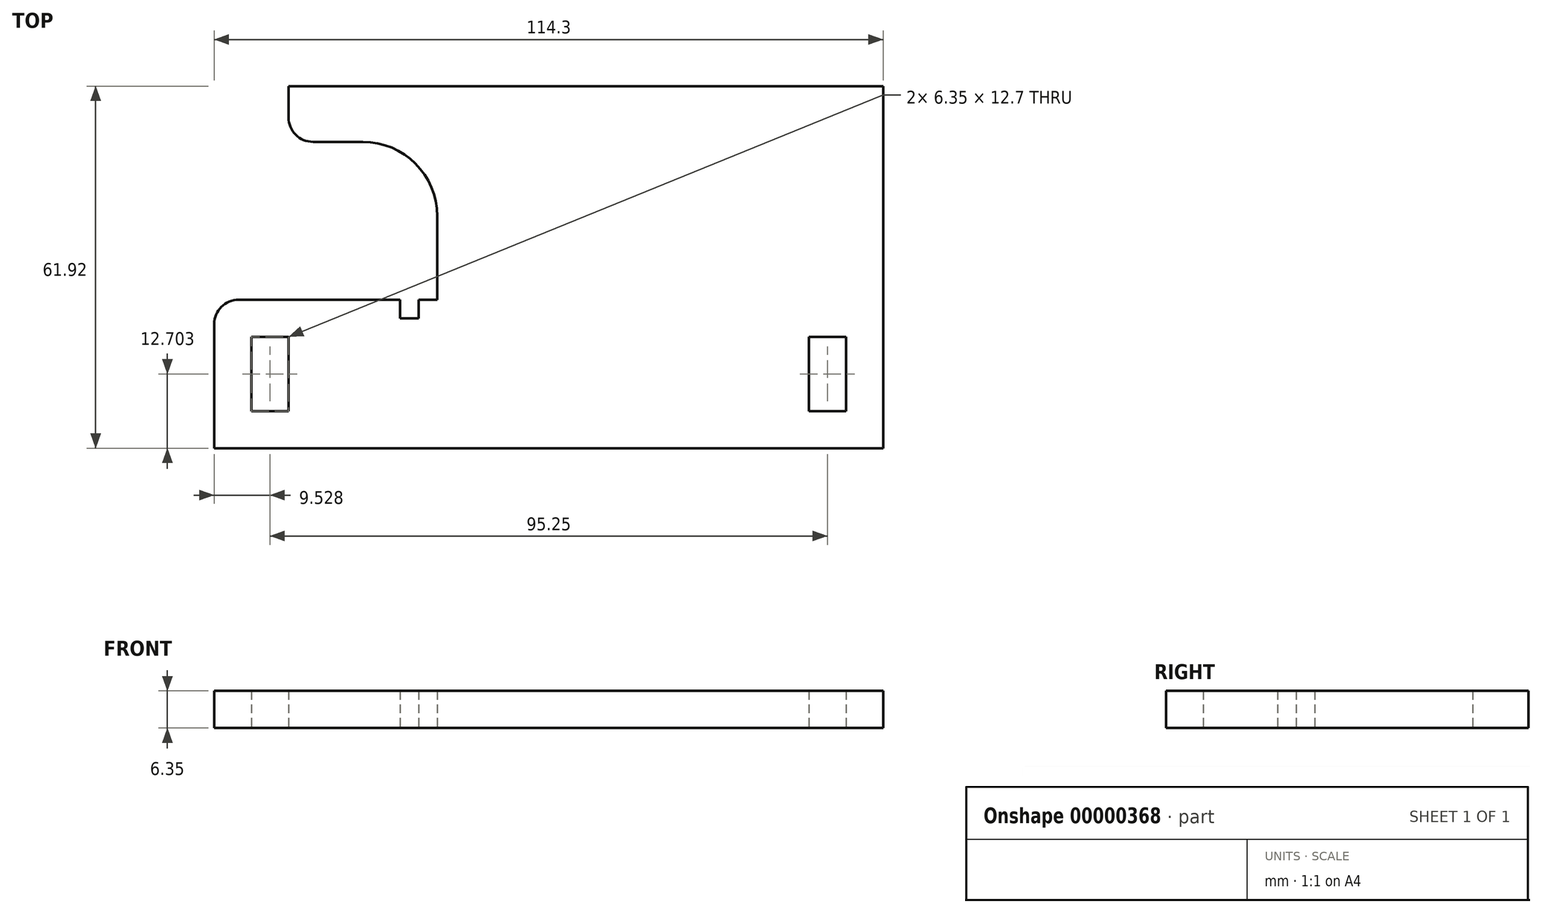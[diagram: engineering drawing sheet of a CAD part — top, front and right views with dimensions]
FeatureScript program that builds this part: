
annotation { "Feature Type Name" : "Feature", "Feature Type Description" : "" }
export const myFeature = defineFeature(function(context is Context, id is Id, definition is map)
    precondition{}
    {
        {
            var Q0;
            Q0=qCreatedBy(makeId("Top.planeOp"),FACE);
            var sketch = newSketch(context, id + "F0", { "sketchPlane" : qUnion([Q0])});
            skLineSegment(sketch, "E0", {"start": v(-52.8, 26.62) * mm, "end": v(48.8, 26.62) * mm});
            skLineSegment(sketch, "E1", {"start": v(48.8, 26.62) * mm, "end": v(48.8, -35.3) * mm});
            skLineSegment(sketch, "E2", {"start": v(48.8, -35.3) * mm, "end": v(-65.5, -35.3) * mm});
            skLineSegment(sketch, "E3", {"start": v(-65.5, -35.3) * mm, "end": v(-65.5, -14.09) * mm});
            skLineSegment(sketch, "E4", {"start": v(-61.3, -9.9) * mm, "end": v(-33.75, -9.9) * mm});
            skLineSegment(sketch, "E5", {"start": v(-27.4, -9.9) * mm, "end": v(-27.4, 4.4) * mm});
            skLineSegment(sketch, "E6", {"start": v(-40.1, 17.1) * mm, "end": v(-48.6, 17.1) * mm});
            skLineSegment(sketch, "E7", {"start": v(-52.8, 21.28) * mm, "end": v(-52.8, 26.62) * mm});
            skPoint(sketch, "E8.visualSharp", {"position": v(-27.4, 17.1) * mm});
            skArc(sketch, "E8.filletArc", {"start": v(-27.4, 4.4) * mm, "mid": v(-31.12, 13.37) * mm, "end": v(-40.1, 17.1) * mm});
            skLineSegment(sketch, "E9.bottom", {"start": v(-59.15, -16.25) * mm, "end": v(-52.8, -16.25) * mm});
            skLineSegment(sketch, "E9.top", {"start": v(-59.15, -28.95) * mm, "end": v(-52.8, -28.95) * mm});
            skLineSegment(sketch, "E9.left", {"start": v(-59.15, -16.25) * mm, "end": v(-59.15, -28.95) * mm});
            skLineSegment(sketch, "E9.right", {"start": v(-52.8, -16.25) * mm, "end": v(-52.8, -28.95) * mm});
            skLineSegment(sketch, "E10", {"start": v(-46, -9.9) * mm, "end": v(-46, -16.25) * mm, "construction": true});
            skLineSegment(sketch, "E11", {"start": v(-55.97, -28.95) * mm, "end": v(-55.97, -35.3) * mm, "construction": true});
            skLineSegment(sketch, "E12.bottom", {"start": v(36.1, -16.25) * mm, "end": v(42.45, -16.25) * mm});
            skLineSegment(sketch, "E12.top", {"start": v(36.1, -28.95) * mm, "end": v(42.45, -28.95) * mm});
            skLineSegment(sketch, "E12.left", {"start": v(36.1, -16.25) * mm, "end": v(36.1, -28.95) * mm});
            skLineSegment(sketch, "E12.right", {"start": v(42.45, -16.25) * mm, "end": v(42.45, -28.95) * mm});
            skLineSegment(sketch, "E13", {"start": v(39.28, -28.95) * mm, "end": v(39.28, -35.3) * mm, "construction": true});
            skLineSegment(sketch, "E14", {"start": v(-30.57, -9.9) * mm, "end": v(-30.57, -13.07) * mm});
            skLineSegment(sketch, "E15", {"start": v(-30.57, -13.07) * mm, "end": v(-33.75, -13.07) * mm});
            skLineSegment(sketch, "E16", {"start": v(-33.75, -13.07) * mm, "end": v(-33.75, -9.9) * mm});
            skLineSegment(sketch, "E17.trimOffspring", {"start": v(-30.57, -9.9) * mm, "end": v(-27.4, -9.9) * mm});
            skPoint(sketch, "E18.visualSharp", {"position": v(-52.8, 17.1) * mm});
            skArc(sketch, "E18.filletArc", {"start": v(-52.8, 21.28) * mm, "mid": v(-51.57, 18.32) * mm, "end": v(-48.6, 17.1) * mm});
            skPoint(sketch, "E19.visualSharp", {"position": v(-65.5, -9.9) * mm});
            skArc(sketch, "E19.filletArc", {"start": v(-61.3, -9.9) * mm, "mid": v(-64.27, -11.12) * mm, "end": v(-65.5, -14.09) * mm});
            skSolve(sketch);
        }
        {
            var Q0;
            Q0=makeQuery(id+"F0.imprint","IMPRINT",FACE,{"disambiguationData":[TD([[makeQuery(id+"F0.imprint","IMPRINT",EDGE,{"derivedFrom":sQuery(id+"F0.wireOp",EDGE,"E0")}),-1.0]])]});
            extrude(context, id + "F1", {"entities" : qUnion([Q0]), "depth" : 6.35 * mm});
        }
    });
